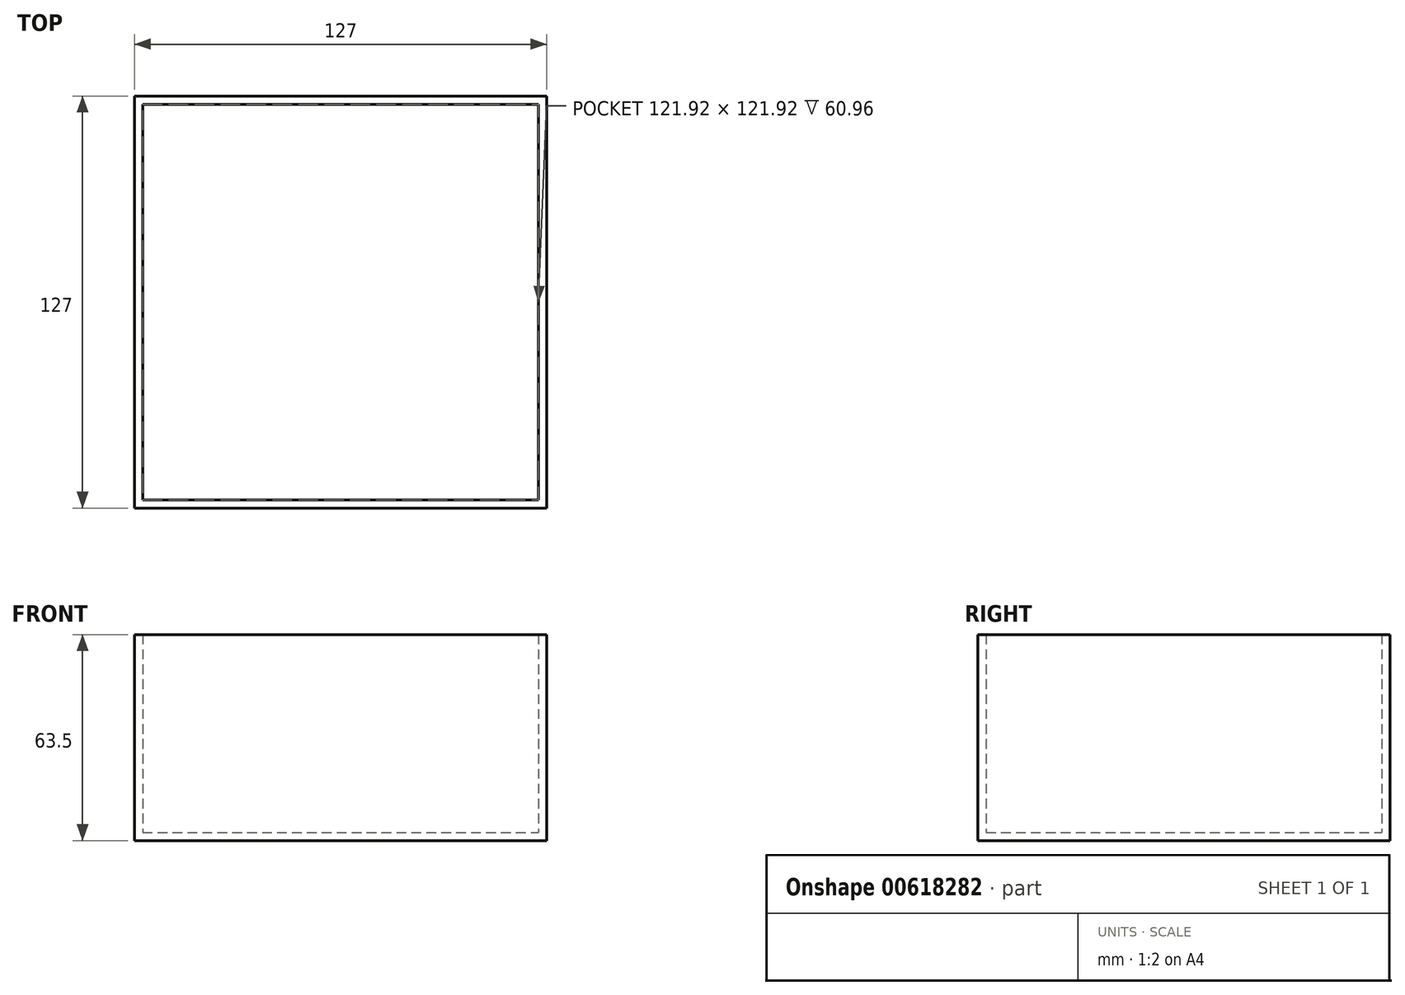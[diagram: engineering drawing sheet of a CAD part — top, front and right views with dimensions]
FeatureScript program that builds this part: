
annotation { "Feature Type Name" : "Feature", "Feature Type Description" : "" }
export const myFeature = defineFeature(function(context is Context, id is Id, definition is map)
    precondition{}
    {
        {
            var Q0;
            Q0=qCreatedBy(makeId("Front.planeOp"),FACE);
            var sketch = newSketch(context, id + "F0", { "sketchPlane" : qUnion([Q0])});
            skLineSegment(sketch, "E0.bottom", {"start": v(-63.5, 63.5) * mm, "end": v(63.5, 63.5) * mm});
            skLineSegment(sketch, "E0.top", {"start": v(-63.5, 0) * mm, "end": v(63.5, 0) * mm});
            skLineSegment(sketch, "E0.left", {"start": v(-63.5, 63.5) * mm, "end": v(-63.5, 0) * mm});
            skLineSegment(sketch, "E0.right", {"start": v(63.5, 63.5) * mm, "end": v(63.5, 0) * mm});
            skSolve(sketch);
        }
        {
            var Q0;
            Q0=makeQuery(id+"F0.imprint","IMPRINT",FACE,{"disambiguationData":[TD([[makeQuery(id+"F0.imprint","IMPRINT",EDGE,{"derivedFrom":sQuery(id+"F0.wireOp",EDGE,"E0.bottom")}),-1.0]])]});
            extrude(context, id + "F1", {"entities" : qUnion([Q0]), "depth" : 63.5 * mm, "offsetDistance" : 25.4 * mm, "hasSecondDirection" : true, "secondDirectionOppositeDirection" : true, "secondDirectionDepth" : 63.5 * mm});
        }
        {
            var Q0;
            Q0=makeQuery(id+"F1.opExtrude","SWEPT_FACE",FACE,{"disambiguationData":[OSD([sQuery(id+"F0.wireOp",EDGE,"E0.bottom")])]});
            shell(context, id + "F2", {"entities" : qUnion([Q0]), "thickness" : 2.54 * mm});
        }
    });
